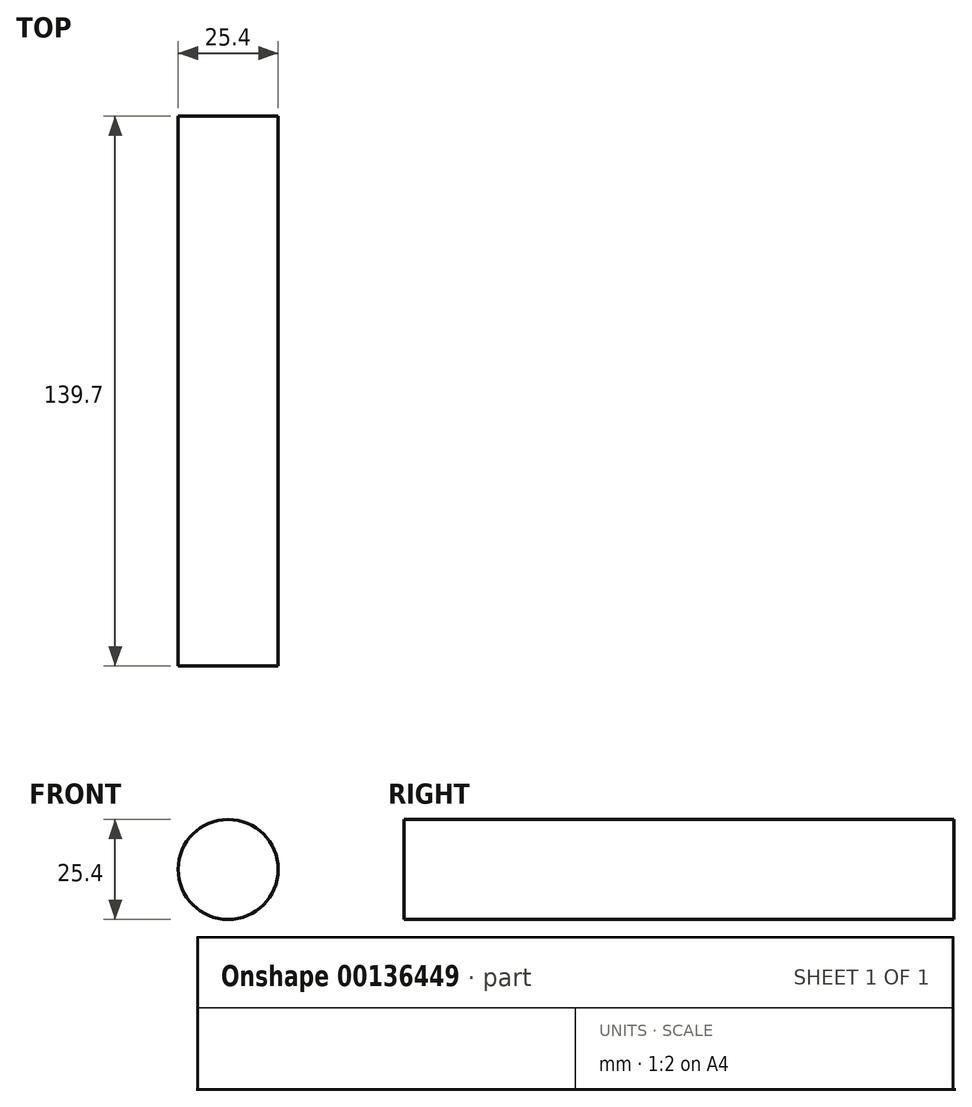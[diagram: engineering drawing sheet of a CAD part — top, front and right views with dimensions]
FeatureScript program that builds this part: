
annotation { "Feature Type Name" : "Feature", "Feature Type Description" : "" }
export const myFeature = defineFeature(function(context is Context, id is Id, definition is map)
    precondition{}
    {
        {
            var Q0;
            Q0=qCreatedBy(makeId("Front.planeOp"),FACE);
            var sketch = newSketch(context, id + "F0", { "sketchPlane" : qUnion([Q0])});
            skCircle(sketch, "E0", {"center": v(0, 0) * mm, "radius": 12.7 * mm});
            skSolve(sketch);
        }
        {
            var Q0;
            Q0=makeQuery(id+"F0.imprint","IMPRINT",FACE,{"disambiguationData":[TD([[makeQuery(id+"F0.imprint","IMPRINT",EDGE,{"derivedFrom":sQuery(id+"F0.wireOp",EDGE,"E0")}),1.0]])]});
            extrude(context, id + "F1", {"entities" : qUnion([Q0]), "oppositeDirection" : true, "depth" : 139.7 * mm});
        }
    });
